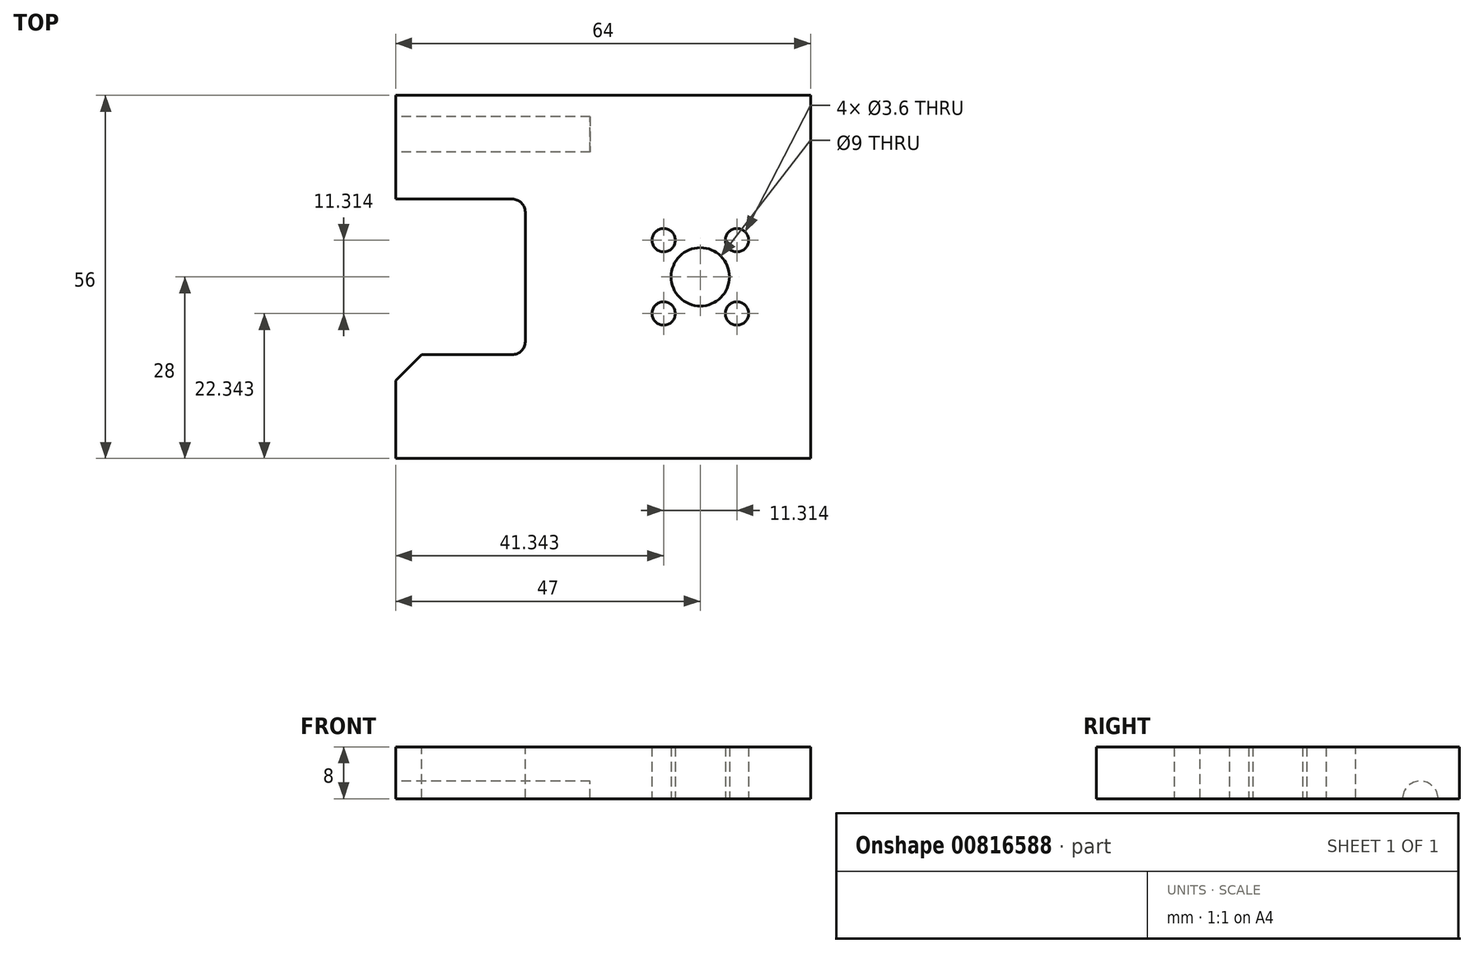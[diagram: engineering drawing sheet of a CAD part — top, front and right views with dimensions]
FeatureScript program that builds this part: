
annotation { "Feature Type Name" : "Feature", "Feature Type Description" : "" }
export const myFeature = defineFeature(function(context is Context, id is Id, definition is map)
    precondition{}
    {
        {
            var Q0;
            Q0=qCreatedBy(makeId("Top.planeOp"),FACE);
            var sketch = newSketch(context, id + "F0", { "sketchPlane" : qUnion([Q0])});
            skLineSegment(sketch, "E0.bottom", {"start": v(-32, 28) * mm, "end": v(32, 28) * mm});
            skLineSegment(sketch, "E0.top", {"start": v(-32, -28) * mm, "end": v(32, -28) * mm});
            skLineSegment(sketch, "E0.left", {"start": v(-32, 28) * mm, "end": v(-32, -28) * mm});
            skLineSegment(sketch, "E0.right", {"start": v(32, 28) * mm, "end": v(32, -28) * mm});
            skLineSegment(sketch, "E1", {"start": v(-32, 0) * mm, "end": v(32, 0) * mm, "construction": true});
            skCircle(sketch, "E2", {"center": v(15, 0) * mm, "radius": 4.5 * mm});
            skCircle(sketch, "E3", {"center": v(15, 0) * mm, "radius": 8 * mm, "construction": true});
            skCircle(sketch, "E4", {"center": v(9.34, 5.66) * mm, "radius": 1.8 * mm});
            skCircle(sketch, "E5.1.0", {"center": v(9.34, -5.66) * mm, "radius": 1.8 * mm});
            skCircle(sketch, "E5.2.0", {"center": v(20.66, -5.66) * mm, "radius": 1.8 * mm});
            skCircle(sketch, "E5.3.0", {"center": v(20.66, 5.66) * mm, "radius": 1.8 * mm});
            skLineSegment(sketch, "E6", {"start": v(9.34, 5.66) * mm, "end": v(20.66, 5.66) * mm, "construction": true});
            skSolve(sketch);
        }
        {
            var Q0;
            Q0=makeQuery(id+"F0.imprint","IMPRINT",FACE,{"disambiguationData":[TD([[makeQuery(id+"F0.imprint","IMPRINT",EDGE,{"derivedFrom":sQuery(id+"F0.wireOp",EDGE,"E0.bottom")}),-1.0]])]});
            extrude(context, id + "F1", {"entities" : qUnion([Q0]), "depth" : 8 * mm, "offsetDistance" : 25 * mm});
        }
        {
            var Q0;
            Q0=makeQuery(id+"F1.opExtrude","SWEPT_FACE",FACE,{"disambiguationData":[OSD([sQuery(id+"F0.wireOp",EDGE,"E0.left")])]});
            var sketch = newSketch(context, id + "F2", { "sketchPlane" : qUnion([Q0])});
            skLineSegment(sketch, "E7", {"start": v(0, 8) * mm, "end": v(0, 0) * mm, "construction": true});
            skLineSegment(sketch, "E8", {"start": v(-28, 0) * mm, "end": v(28, 0) * mm, "construction": true});
            skCircle(sketch, "E9", {"center": v(-22, 0) * mm, "radius": 2.72 * mm});
            skCircle(sketch, "E10.MirrorC", {"center": v(22, 0) * mm, "radius": 2.72 * mm});
            skSolve(sketch);
        }
        {
            var Q0;
            {var subQ0=sQuery(id+"F2.wireOp",EDGE,"E9");var subQ1=makeQuery(id+"F1.opExtrude","CAP_EDGE",EDGE,{"disambiguationData":[OSD([sQuery(id+"F0.wireOp",EDGE,"E0.left")])],"isStart":true});var subQ2=makeQuery(id+"F2.imprint","INTERSECT",VERTEX,{"disambiguationData":[OD(0.0)],"derivedFrom":[subQ1,subQ0]});Q0=makeQuery(id+"F2.imprint","IMPRINT",FACE,{"disambiguationData":[TD([[makeQuery(id+"F2.imprint","IMPRINT",EDGE,{"disambiguationData":[TD([[subQ2,1.0]])],"derivedFrom":subQ0}),1.0]])]});}
            var Q1;
            {var subQ0=sQuery(id+"F2.wireOp",EDGE,"E10.MirrorC");var subQ1=makeQuery(id+"F1.opExtrude","CAP_EDGE",EDGE,{"disambiguationData":[OSD([sQuery(id+"F0.wireOp",EDGE,"E0.left")])],"isStart":true});var subQ2=makeQuery(id+"F2.imprint","INTERSECT",VERTEX,{"disambiguationData":[OD(0.0)],"derivedFrom":[subQ1,subQ0]});Q1=makeQuery(id+"F2.imprint","IMPRINT",FACE,{"disambiguationData":[TD([[makeQuery(id+"F2.imprint","IMPRINT",EDGE,{"disambiguationData":[TD([[subQ2,1.0]])],"derivedFrom":subQ0}),-1.0]])]});}
            extrude(context, id + "F3", {"entities" : qUnion([Q0, Q1]), "operationType" : NewBodyOperationType.REMOVE, "oppositeDirection" : true, "depth" : 30 * mm, "offsetDistance" : 25 * mm});
        }
        {
            var Q0;
            Q0=makeQuery(id+"F1.opExtrude","CAP_FACE",FACE,{"disambiguationData":[OSD([sQuery(id+"F0.wireOp",EDGE,"E0.bottom"),sQuery(id+"F0.wireOp",EDGE,"E0.top"),sQuery(id+"F0.wireOp",EDGE,"E0.left"),sQuery(id+"F0.wireOp",EDGE,"E0.right"),sQuery(id+"F0.wireOp",EDGE,"E2"),sQuery(id+"F0.wireOp",EDGE,"E4"),sQuery(id+"F0.wireOp",EDGE,"E5.1.0"),sQuery(id+"F0.wireOp",EDGE,"E5.2.0"),sQuery(id+"F0.wireOp",EDGE,"E5.3.0")])],"isStart":false});
            var sketch = newSketch(context, id + "F4", { "sketchPlane" : qUnion([Q0])});
            skLineSegment(sketch, "E11.bottom", {"start": v(-32, 12) * mm, "end": v(-12, 12) * mm});
            skLineSegment(sketch, "E11.top", {"start": v(-32, -12) * mm, "end": v(-12, -12) * mm});
            skLineSegment(sketch, "E11.left", {"start": v(-32, 12) * mm, "end": v(-32, -12) * mm});
            skLineSegment(sketch, "E11.right", {"start": v(-12, 12) * mm, "end": v(-12, -12) * mm});
            skLineSegment(sketch, "E12", {"start": v(-32, 0) * mm, "end": v(-20.67, 0) * mm, "construction": true});
            skSolve(sketch);
        }
        {
            var Q0;
            Q0=makeQuery(id+"F4.imprint","IMPRINT",FACE,{"disambiguationData":[TD([[makeQuery(id+"F4.imprint","IMPRINT",EDGE,{"derivedFrom":sQuery(id+"F4.wireOp",EDGE,"E11.bottom")}),-1.0]])]});
            extrude(context, id + "F5", {"entities" : qUnion([Q0]), "operationType" : NewBodyOperationType.REMOVE, "oppositeDirection" : true, "depth" : 25 * mm, "offsetDistance" : 25 * mm});
        }
        {
            var Q0;
            Q0=makeQuery(id+"F5.boolean.opBoolean","COPY",EDGE,{"derivedFrom":makeQuery(id+"F5.opExtrude","SWEPT_EDGE",EDGE,{"disambiguationData":[OSD([sQuery(id+"F0.wireOp",EDGE,"E0.left"),sQuery(id+"F4.wireOp",EDGE,"E11.bottom"),sQuery(id+"F4.wireOp",EDGE,"E11.left")])]})});
            var Q1;
            Q1=makeQuery(id+"F5.boolean.opBoolean","COPY",EDGE,{"derivedFrom":makeQuery(id+"F5.opExtrude","SWEPT_EDGE",EDGE,{"disambiguationData":[OSD([sQuery(id+"F0.wireOp",EDGE,"E0.left"),sQuery(id+"F4.wireOp",EDGE,"E11.top"),sQuery(id+"F4.wireOp",EDGE,"E11.left")])]})});
            chamfer(context, id + "F6", {"entities" : qUnion([Q0, Q1]), "width" : 4 * mm, "tangentPropagation" : true});
        }
        {
            var Q0;
            Q0=makeQuery(id+"F5.boolean.opBoolean","COPY",EDGE,{"derivedFrom":makeQuery(id+"F5.opExtrude","SWEPT_EDGE",EDGE,{"disambiguationData":[OSD([sQuery(id+"F4.wireOp",EDGE,"E11.bottom"),sQuery(id+"F4.wireOp",EDGE,"E11.right")])]})});
            var Q1;
            Q1=makeQuery(id+"F5.boolean.opBoolean","COPY",EDGE,{"derivedFrom":makeQuery(id+"F5.opExtrude","SWEPT_EDGE",EDGE,{"disambiguationData":[OSD([sQuery(id+"F4.wireOp",EDGE,"E11.top"),sQuery(id+"F4.wireOp",EDGE,"E11.right")])]})});
            fillet(context, id + "F7", {"entities" : qUnion([Q0, Q1]), "radius" : 2 * mm, "tangentPropagation" : true, "allowEdgeOverflow" : false});
        }
    });
